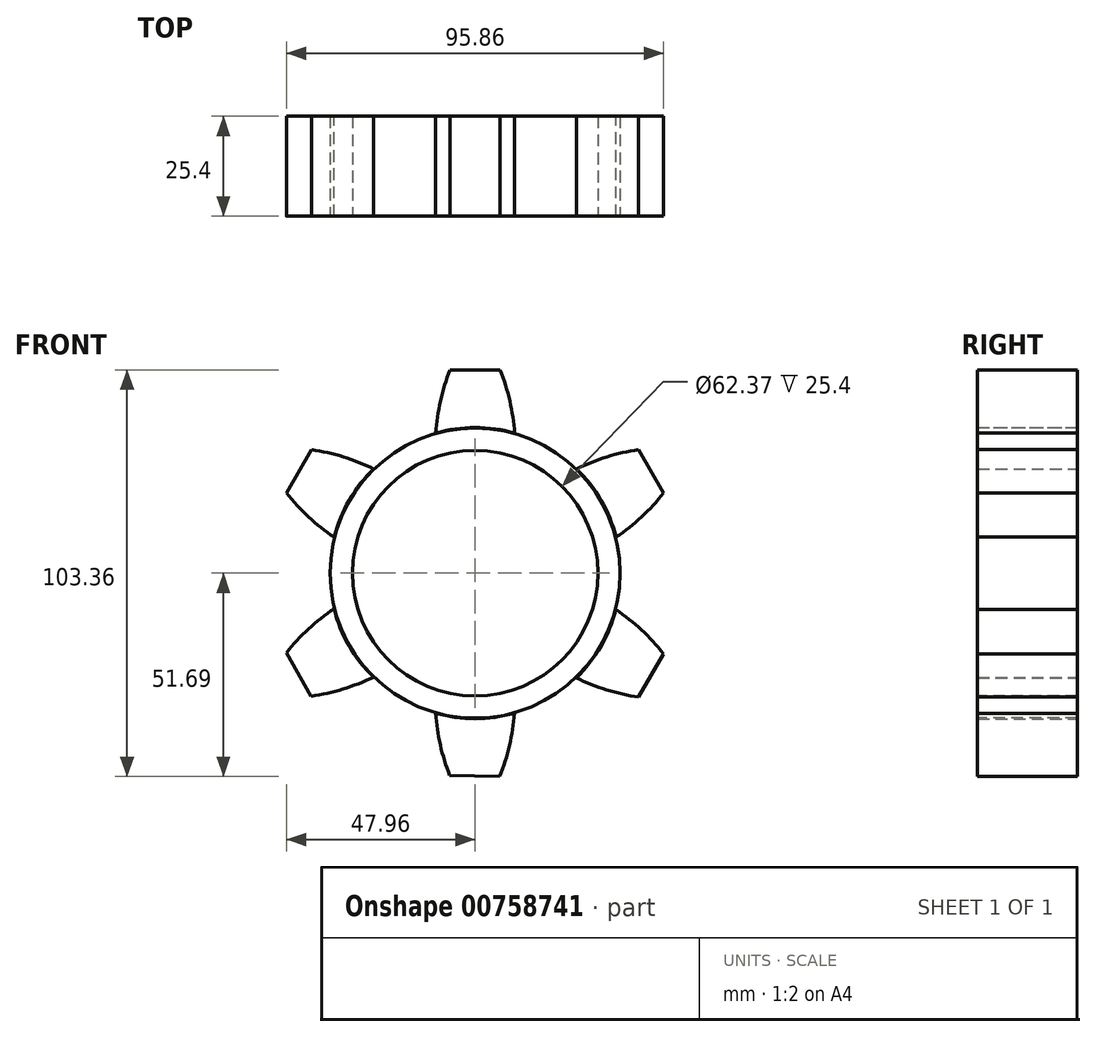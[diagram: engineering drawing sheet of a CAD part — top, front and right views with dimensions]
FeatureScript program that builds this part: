
annotation { "Feature Type Name" : "Feature", "Feature Type Description" : "" }
export const myFeature = defineFeature(function(context is Context, id is Id, definition is map)
    precondition{}
    {
        {
            var Q0;
            Q0=qCreatedBy(makeId("Front.planeOp"),FACE);
            var sketch = newSketch(context, id + "F0", { "sketchPlane" : qUnion([Q0])});
            skCircle(sketch, "E0", {"center": v(0, 0) * mm, "radius": 36.98 * mm});
            skLineSegment(sketch, "E1", {"start": v(-6.35, 36.43) * mm, "end": v(-6.35, 51.67) * mm});
            skLineSegment(sketch, "E2", {"start": v(-6.35, 51.67) * mm, "end": v(6.35, 51.67) * mm});
            skLineSegment(sketch, "E3", {"start": v(6.35, 51.67) * mm, "end": v(6.35, 36.43) * mm});
            skLineSegment(sketch, "E4", {"start": v(-28.35, 23.74) * mm, "end": v(-41.54, 31.37) * mm});
            skLineSegment(sketch, "E5", {"start": v(-41.54, 31.37) * mm, "end": v(-47.9, 20.38) * mm});
            skLineSegment(sketch, "E6", {"start": v(-47.9, 20.38) * mm, "end": v(-34.71, 12.75) * mm});
            skLineSegment(sketch, "E7", {"start": v(-34.75, -12.65) * mm, "end": v(-47.96, -20.25) * mm});
            skLineSegment(sketch, "E8", {"start": v(-47.96, -20.25) * mm, "end": v(-41.63, -31.26) * mm});
            skLineSegment(sketch, "E9", {"start": v(-41.63, -31.26) * mm, "end": v(-28.42, -23.66) * mm});
            skLineSegment(sketch, "E10", {"start": v(41.54, 31.37) * mm, "end": v(28.35, 23.74) * mm});
            skLineSegment(sketch, "E11", {"start": v(41.54, 31.37) * mm, "end": v(47.9, 20.38) * mm});
            skLineSegment(sketch, "E12", {"start": v(47.9, 20.38) * mm, "end": v(34.71, 12.75) * mm});
            skLineSegment(sketch, "E13", {"start": v(-6.45, -36.41) * mm, "end": v(-6.45, -51.45) * mm});
            skLineSegment(sketch, "E14", {"start": v(-6.45, -51.45) * mm, "end": v(6.25, -51.69) * mm});
            skLineSegment(sketch, "E15", {"start": v(6.25, -51.69) * mm, "end": v(6.25, -36.45) * mm});
            skLineSegment(sketch, "E16", {"start": v(28.29, -23.82) * mm, "end": v(41.46, -31.49) * mm});
            skLineSegment(sketch, "E17", {"start": v(41.46, -31.49) * mm, "end": v(47.85, -20.51) * mm});
            skLineSegment(sketch, "E18", {"start": v(47.85, -20.51) * mm, "end": v(34.68, -12.85) * mm});
            skArc(sketch, "E19", {"start": v(-6.35, 51.67) * mm, "mid": v(-9.77, 25.02) * mm, "end": v(0, 0) * mm});
            skArc(sketch, "E20", {"start": v(0, 0) * mm, "mid": v(9.77, 25.02) * mm, "end": v(6.35, 51.67) * mm});
            skArc(sketch, "E21", {"start": v(41.54, 31.37) * mm, "mid": v(16.77, 21) * mm, "end": v(0, 0) * mm});
            skArc(sketch, "E22", {"start": v(-47.9, 20.38) * mm, "mid": v(-26.55, 4.07) * mm, "end": v(0, 0) * mm});
            skArc(sketch, "E23", {"start": v(0, 0) * mm, "mid": v(-16.77, 21) * mm, "end": v(-41.54, 31.37) * mm});
            skArc(sketch, "E24", {"start": v(0, 0) * mm, "mid": v(26.55, 4.07) * mm, "end": v(47.9, 20.38) * mm});
            skArc(sketch, "E25", {"start": v(47.85, -20.51) * mm, "mid": v(26.54, -4.15) * mm, "end": v(0, 0) * mm});
            skArc(sketch, "E26", {"start": v(0, 0) * mm, "mid": v(16.7, -21.04) * mm, "end": v(41.46, -31.49) * mm});
            skArc(sketch, "E27", {"start": v(6.25, -51.69) * mm, "mid": v(9.73, -25.05) * mm, "end": v(0, 0) * mm});
            skArc(sketch, "E28", {"start": v(0, 0) * mm, "mid": v(-9.77, -24.9) * mm, "end": v(-6.45, -51.45) * mm});
            skArc(sketch, "E29", {"start": v(0, 0) * mm, "mid": v(-26.57, -4) * mm, "end": v(-47.96, -20.25) * mm});
            skArc(sketch, "E30", {"start": v(-41.63, -31.26) * mm, "mid": v(-16.82, -20.95) * mm, "end": v(0, 0) * mm});
            skSolve(sketch);
        }
        {
            var Q0;
            {var subQ0=sQuery(id+"F0.wireOp",EDGE,"E1");Q0=makeQuery(id+"F0.imprint","IMPRINT",FACE,{"disambiguationData":[TD([[makeQuery(id+"F0.imprint","IMPRINT",EDGE,{"derivedFrom":subQ0}),1.0]])]});}
            var Q1;
            {var subQ0=sQuery(id+"F0.wireOp",EDGE,"E1");Q1=makeQuery(id+"F0.imprint","IMPRINT",FACE,{"disambiguationData":[TD([[makeQuery(id+"F0.imprint","IMPRINT",EDGE,{"derivedFrom":subQ0}),-1.0]])]});}
            var Q2;
            {var subQ0=sQuery(id+"F0.wireOp",EDGE,"E3");Q2=makeQuery(id+"F0.imprint","IMPRINT",FACE,{"disambiguationData":[TD([[makeQuery(id+"F0.imprint","IMPRINT",EDGE,{"derivedFrom":subQ0}),1.0]])]});}
            var Q3;
            {var subQ0=sQuery(id+"F0.wireOp",EDGE,"E10");Q3=makeQuery(id+"F0.imprint","IMPRINT",FACE,{"disambiguationData":[TD([[makeQuery(id+"F0.imprint","IMPRINT",EDGE,{"derivedFrom":subQ0}),-1.0]])]});}
            var Q4;
            {var subQ0=sQuery(id+"F0.wireOp",EDGE,"E10");Q4=makeQuery(id+"F0.imprint","IMPRINT",FACE,{"disambiguationData":[TD([[makeQuery(id+"F0.imprint","IMPRINT",EDGE,{"derivedFrom":subQ0}),1.0]])]});}
            var Q5;
            {var subQ0=sQuery(id+"F0.wireOp",EDGE,"E12");Q5=makeQuery(id+"F0.imprint","IMPRINT",FACE,{"disambiguationData":[TD([[makeQuery(id+"F0.imprint","IMPRINT",EDGE,{"derivedFrom":subQ0}),1.0]])]});}
            var Q6;
            {var subQ0=sQuery(id+"F0.wireOp",EDGE,"E18");Q6=makeQuery(id+"F0.imprint","IMPRINT",FACE,{"disambiguationData":[TD([[makeQuery(id+"F0.imprint","IMPRINT",EDGE,{"derivedFrom":subQ0}),-1.0]])]});}
            var Q7;
            {var subQ0=sQuery(id+"F0.wireOp",EDGE,"E16");Q7=makeQuery(id+"F0.imprint","IMPRINT",FACE,{"disambiguationData":[TD([[makeQuery(id+"F0.imprint","IMPRINT",EDGE,{"derivedFrom":subQ0}),1.0]])]});}
            var Q8;
            {var subQ0=sQuery(id+"F0.wireOp",EDGE,"E16");Q8=makeQuery(id+"F0.imprint","IMPRINT",FACE,{"disambiguationData":[TD([[makeQuery(id+"F0.imprint","IMPRINT",EDGE,{"derivedFrom":subQ0}),-1.0]])]});}
            var Q9;
            {var subQ0=sQuery(id+"F0.wireOp",EDGE,"E15");Q9=makeQuery(id+"F0.imprint","IMPRINT",FACE,{"disambiguationData":[TD([[makeQuery(id+"F0.imprint","IMPRINT",EDGE,{"derivedFrom":subQ0}),-1.0]])]});}
            var Q10;
            {var subQ0=sQuery(id+"F0.wireOp",EDGE,"E13");Q10=makeQuery(id+"F0.imprint","IMPRINT",FACE,{"disambiguationData":[TD([[makeQuery(id+"F0.imprint","IMPRINT",EDGE,{"derivedFrom":subQ0}),-1.0]])]});}
            var Q11;
            {var subQ0=sQuery(id+"F0.wireOp",EDGE,"E13");Q11=makeQuery(id+"F0.imprint","IMPRINT",FACE,{"disambiguationData":[TD([[makeQuery(id+"F0.imprint","IMPRINT",EDGE,{"derivedFrom":subQ0}),1.0]])]});}
            var Q12;
            {var subQ0=sQuery(id+"F0.wireOp",EDGE,"E7");Q12=makeQuery(id+"F0.imprint","IMPRINT",FACE,{"disambiguationData":[TD([[makeQuery(id+"F0.imprint","IMPRINT",EDGE,{"derivedFrom":subQ0}),-1.0]])]});}
            var Q13;
            {var subQ0=sQuery(id+"F0.wireOp",EDGE,"E9");Q13=makeQuery(id+"F0.imprint","IMPRINT",FACE,{"disambiguationData":[TD([[makeQuery(id+"F0.imprint","IMPRINT",EDGE,{"derivedFrom":subQ0}),-1.0]])]});}
            var Q14;
            {var subQ0=sQuery(id+"F0.wireOp",EDGE,"E7");Q14=makeQuery(id+"F0.imprint","IMPRINT",FACE,{"disambiguationData":[TD([[makeQuery(id+"F0.imprint","IMPRINT",EDGE,{"derivedFrom":subQ0}),1.0]])]});}
            var Q15;
            {var subQ0=sQuery(id+"F0.wireOp",EDGE,"E6");Q15=makeQuery(id+"F0.imprint","IMPRINT",FACE,{"disambiguationData":[TD([[makeQuery(id+"F0.imprint","IMPRINT",EDGE,{"derivedFrom":subQ0}),-1.0]])]});}
            var Q16;
            {var subQ0=sQuery(id+"F0.wireOp",EDGE,"E4");Q16=makeQuery(id+"F0.imprint","IMPRINT",FACE,{"disambiguationData":[TD([[makeQuery(id+"F0.imprint","IMPRINT",EDGE,{"derivedFrom":subQ0}),-1.0]])]});}
            var Q17;
            {var subQ0=sQuery(id+"F0.wireOp",EDGE,"E4");Q17=makeQuery(id+"F0.imprint","IMPRINT",FACE,{"disambiguationData":[TD([[makeQuery(id+"F0.imprint","IMPRINT",EDGE,{"derivedFrom":subQ0}),1.0]])]});}
            extrude(context, id + "F1", {"entities" : qUnion([Q0, Q1, Q2, Q3, Q4, Q5, Q6, Q7, Q8, Q9, Q10, Q11, Q12, Q13, Q14, Q15, Q16, Q17]), "depth" : 25.4 * mm, "offsetDistance" : 25.4 * mm});
        }
        {
            var Q0;
            Q0=makeQuery(id+"F1.opExtrude","CAP_FACE",FACE,{"disambiguationData":[OSD([sQuery(id+"F0.wireOp",EDGE,"E0"),sQuery(id+"F0.wireOp",EDGE,"E5"),sQuery(id+"F0.wireOp",EDGE,"E22"),sQuery(id+"F0.wireOp",EDGE,"E23")])],"isStart":false});
            var sketch = newSketch(context, id + "F2", { "sketchPlane" : qUnion([Q0])});
            skCircle(sketch, "E31", {"center": v(0, 0) * mm, "radius": 36.84 * mm});
            skSolve(sketch);
        }
        {
            var Q0;
            Q0=makeQuery(id+"F2.imprint","IMPRINT",FACE,{"disambiguationData":[TD([[makeQuery(id+"F2.imprint","IMPRINT",EDGE,{"derivedFrom":sQuery(id+"F2.wireOp",EDGE,"E31")}),1.0]])]});
            extrude(context, id + "F3", {"entities" : qUnion([Q0]), "oppositeDirection" : true, "depth" : 25.4 * mm, "offsetDistance" : 25.4 * mm});
        }
        {
            var Q0;
            Q0=makeQuery(id+"F3.opExtrude","CAP_FACE",FACE,{"disambiguationData":[OSD([sQuery(id+"F2.wireOp",EDGE,"E31")])],"isStart":true});
            var sketch = newSketch(context, id + "F4", { "sketchPlane" : qUnion([Q0])});
            skCircle(sketch, "E32", {"center": v(0, 0) * mm, "radius": 31.19 * mm});
            skSolve(sketch);
        }
        {
            var Q0;
            Q0 = qSketchRegion(id + "F4", true);
            extrude(context, id + "F5", {"entities" : qUnion([Q0]), "operationType" : NewBodyOperationType.REMOVE, "oppositeDirection" : true, "depth" : 44.7 * mm, "offsetDistance" : 25.4 * mm});
        }
    });
